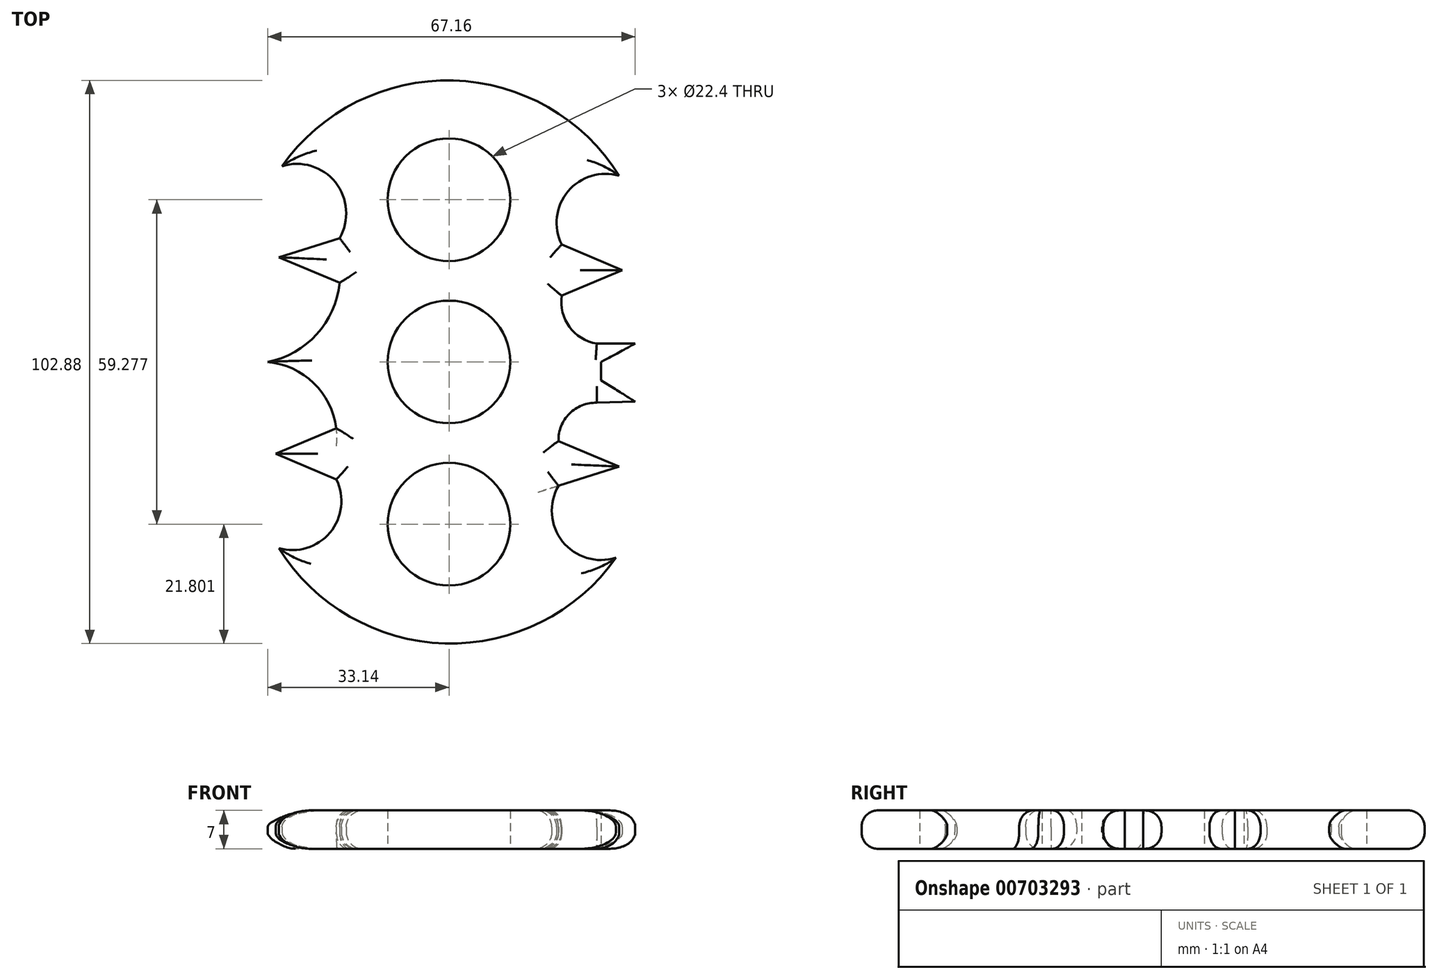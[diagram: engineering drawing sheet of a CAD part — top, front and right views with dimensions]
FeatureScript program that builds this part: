
annotation { "Feature Type Name" : "Feature", "Feature Type Description" : "" }
export const myFeature = defineFeature(function(context is Context, id is Id, definition is map)
    precondition{}
    {
        {
            var Q0;
            Q0=qCreatedBy(makeId("Top.planeOp"),FACE);
            var sketch = newSketch(context, id + "F0", { "sketchPlane" : qUnion([Q0])});
            skCircle(sketch, "E0", {"center": v(0, 0) * mm, "radius": 11.2 * mm});
            skCircle(sketch, "E1", {"center": v(0, 29.64) * mm, "radius": 11.2 * mm});
            skCircle(sketch, "E2.1.1", {"center": v(0, -29.64) * mm, "radius": 11.2 * mm});
            skArc(sketch, "E3", {"start": v(31.1, 34.02) * mm, "mid": v(0.76, 51.42) * mm, "end": v(-30.51, 35.77) * mm});
            skArc(sketch, "E4", {"start": v(-20, 22.63) * mm, "mid": v(-20.75, 32.8) * mm, "end": v(-30.51, 35.77) * mm});
            skLineSegment(sketch, "E5", {"start": v(-20, 22.63) * mm, "end": v(-31.1, 19.13) * mm});
            skLineSegment(sketch, "E6", {"start": v(-31.1, 19.13) * mm, "end": v(-20, 14.45) * mm});
            skArc(sketch, "E7", {"start": v(-33.14, 0) * mm, "mid": v(-24.17, 5.05) * mm, "end": v(-20, 14.45) * mm});
            skArc(sketch, "E8.1.0", {"start": v(-31.1, -34.02) * mm, "mid": v(-0.76, -51.42) * mm, "end": v(30.51, -35.77) * mm});
            skArc(sketch, "E8.1.1", {"start": v(20, -22.63) * mm, "mid": v(20.75, -32.8) * mm, "end": v(30.51, -35.77) * mm});
            skLineSegment(sketch, "E8.1.2", {"start": v(20, -22.63) * mm, "end": v(31.1, -19.13) * mm});
            skLineSegment(sketch, "E8.1.3", {"start": v(31.1, -19.13) * mm, "end": v(20, -14.45) * mm});
            skArc(sketch, "E9", {"start": v(-20.59, -12.12) * mm, "mid": v(-24.73, -3.85) * mm, "end": v(-33.14, 0) * mm});
            skLineSegment(sketch, "E10", {"start": v(-20.59, -12.12) * mm, "end": v(-31.68, -16.8) * mm});
            skLineSegment(sketch, "E11", {"start": v(-31.68, -16.8) * mm, "end": v(-20.59, -21.46) * mm});
            skArc(sketch, "E12", {"start": v(-31.1, -34.02) * mm, "mid": v(-21.74, -31.17) * mm, "end": v(-20.59, -21.46) * mm});
            skLineSegment(sketch, "E13.1.0", {"start": v(20.59, 12.12) * mm, "end": v(31.68, 16.8) * mm});
            skLineSegment(sketch, "E13.1.1", {"start": v(31.68, 16.8) * mm, "end": v(20.59, 21.46) * mm});
            skArc(sketch, "E13.1.2", {"start": v(31.1, 34.02) * mm, "mid": v(21.74, 31.17) * mm, "end": v(20.59, 21.46) * mm});
            skArc(sketch, "E14", {"start": v(20.59, 12.12) * mm, "mid": v(22, 6.42) * mm, "end": v(27.01, 3.36) * mm});
            skArc(sketch, "E15", {"start": v(27.01, -7.45) * mm, "mid": v(22.01, -9.45) * mm, "end": v(20, -14.45) * mm});
            skLineSegment(sketch, "E16", {"start": v(27.01, 3.36) * mm, "end": v(34.02, 3.36) * mm});
            skLineSegment(sketch, "E17", {"start": v(34.02, 3.36) * mm, "end": v(27.8, 0) * mm});
            skLineSegment(sketch, "E18", {"start": v(27.8, 0) * mm, "end": v(27.8, -3.36) * mm});
            skLineSegment(sketch, "E19", {"start": v(27.8, -3.36) * mm, "end": v(34.02, -7.26) * mm});
            skLineSegment(sketch, "E20", {"start": v(34.02, -7.26) * mm, "end": v(27.01, -7.45) * mm});
            skSolve(sketch);
        }
        {
            var Q0;
            Q0=makeQuery(id+"F0.imprint","IMPRINT",FACE,{"disambiguationData":[TD([[makeQuery(id+"F0.imprint","IMPRINT",EDGE,{"derivedFrom":sQuery(id+"F0.wireOp",EDGE,"E0")}),-1.0]])]});
            extrude(context, id + "F1", {"entities" : qUnion([Q0]), "depth" : 7 * mm, "offsetDistance" : 25 * mm});
        }
        {
            var Q0;
            Q0=makeQuery(id+"F1.opExtrude","CAP_EDGE",EDGE,{"disambiguationData":[OSD([sQuery(id+"F0.wireOp",EDGE,"E3")])],"isStart":false});
            var Q1;
            Q1=makeQuery(id+"F1.opExtrude","CAP_EDGE",EDGE,{"disambiguationData":[OSD([sQuery(id+"F0.wireOp",EDGE,"E8.1.0")])],"isStart":false});
            var Q2;
            Q2=makeQuery(id+"F1.opExtrude","CAP_EDGE",EDGE,{"disambiguationData":[OSD([sQuery(id+"F0.wireOp",EDGE,"E12")])],"isStart":false});
            var Q3;
            Q3=makeQuery(id+"F1.opExtrude","CAP_EDGE",EDGE,{"disambiguationData":[OSD([sQuery(id+"F0.wireOp",EDGE,"E8.1.1")])],"isStart":false});
            var Q4;
            Q4=makeQuery(id+"F1.opExtrude","CAP_EDGE",EDGE,{"disambiguationData":[OSD([sQuery(id+"F0.wireOp",EDGE,"E14")])],"isStart":false});
            var Q5;
            Q5=makeQuery(id+"F1.opExtrude","CAP_EDGE",EDGE,{"disambiguationData":[OSD([sQuery(id+"F0.wireOp",EDGE,"E15")])],"isStart":false});
            var Q6;
            Q6=makeQuery(id+"F1.opExtrude","CAP_EDGE",EDGE,{"disambiguationData":[OSD([sQuery(id+"F0.wireOp",EDGE,"E16")])],"isStart":false});
            var Q7;
            Q7=makeQuery(id+"F1.opExtrude","CAP_EDGE",EDGE,{"disambiguationData":[OSD([sQuery(id+"F0.wireOp",EDGE,"E13.1.2")])],"isStart":false});
            var Q8;
            Q8=makeQuery(id+"F1.opExtrude","CAP_EDGE",EDGE,{"disambiguationData":[OSD([sQuery(id+"F0.wireOp",EDGE,"E20")])],"isStart":false});
            var Q9;
            Q9=makeQuery(id+"F1.opExtrude","CAP_EDGE",EDGE,{"disambiguationData":[OSD([sQuery(id+"F0.wireOp",EDGE,"E9")])],"isStart":false});
            var Q10;
            Q10=makeQuery(id+"F1.opExtrude","CAP_EDGE",EDGE,{"disambiguationData":[OSD([sQuery(id+"F0.wireOp",EDGE,"E7")])],"isStart":false});
            var Q11;
            Q11=makeQuery(id+"F1.opExtrude","CAP_EDGE",EDGE,{"disambiguationData":[OSD([sQuery(id+"F0.wireOp",EDGE,"E6")])],"isStart":false});
            var Q12;
            Q12=makeQuery(id+"F1.opExtrude","CAP_EDGE",EDGE,{"disambiguationData":[OSD([sQuery(id+"F0.wireOp",EDGE,"E4")])],"isStart":false});
            var Q13;
            Q13=makeQuery(id+"F1.opExtrude","CAP_EDGE",EDGE,{"disambiguationData":[OSD([sQuery(id+"F0.wireOp",EDGE,"E5")])],"isStart":false});
            var Q14;
            Q14=makeQuery(id+"F1.opExtrude","CAP_EDGE",EDGE,{"disambiguationData":[OSD([sQuery(id+"F0.wireOp",EDGE,"E10")])],"isStart":false});
            var Q15;
            Q15=makeQuery(id+"F1.opExtrude","CAP_EDGE",EDGE,{"disambiguationData":[OSD([sQuery(id+"F0.wireOp",EDGE,"E8.1.3")])],"isStart":false});
            var Q16;
            Q16=makeQuery(id+"F1.opExtrude","CAP_EDGE",EDGE,{"disambiguationData":[OSD([sQuery(id+"F0.wireOp",EDGE,"E11")])],"isStart":false});
            var Q17;
            Q17=makeQuery(id+"F1.opExtrude","CAP_EDGE",EDGE,{"disambiguationData":[OSD([sQuery(id+"F0.wireOp",EDGE,"E8.1.2")])],"isStart":false});
            var Q18;
            Q18=makeQuery(id+"F1.opExtrude","CAP_EDGE",EDGE,{"disambiguationData":[OSD([sQuery(id+"F0.wireOp",EDGE,"E13.1.1")])],"isStart":false});
            var Q19;
            Q19=makeQuery(id+"F1.opExtrude","CAP_EDGE",EDGE,{"disambiguationData":[OSD([sQuery(id+"F0.wireOp",EDGE,"E13.1.0")])],"isStart":false});
            var Q20;
            Q20=makeQuery(id+"F1.opExtrude","CAP_EDGE",EDGE,{"disambiguationData":[OSD([sQuery(id+"F0.wireOp",EDGE,"E8.1.0")])],"isStart":true});
            var Q21;
            Q21=makeQuery(id+"F1.opExtrude","CAP_EDGE",EDGE,{"disambiguationData":[OSD([sQuery(id+"F0.wireOp",EDGE,"E3")])],"isStart":true});
            var Q22;
            Q22=makeQuery(id+"F1.opExtrude","CAP_EDGE",EDGE,{"disambiguationData":[OSD([sQuery(id+"F0.wireOp",EDGE,"E20")])],"isStart":true});
            var Q23;
            Q23=makeQuery(id+"F1.opExtrude","CAP_EDGE",EDGE,{"disambiguationData":[OSD([sQuery(id+"F0.wireOp",EDGE,"E15")])],"isStart":true});
            var Q24;
            Q24=makeQuery(id+"F1.opExtrude","CAP_EDGE",EDGE,{"disambiguationData":[OSD([sQuery(id+"F0.wireOp",EDGE,"E14")])],"isStart":true});
            var Q25;
            Q25=makeQuery(id+"F1.opExtrude","CAP_EDGE",EDGE,{"disambiguationData":[OSD([sQuery(id+"F0.wireOp",EDGE,"E16")])],"isStart":true});
            var Q26;
            Q26=makeQuery(id+"F1.opExtrude","CAP_EDGE",EDGE,{"disambiguationData":[OSD([sQuery(id+"F0.wireOp",EDGE,"E8.1.3")])],"isStart":true});
            var Q27;
            Q27=makeQuery(id+"F1.opExtrude","CAP_EDGE",EDGE,{"disambiguationData":[OSD([sQuery(id+"F0.wireOp",EDGE,"E8.1.1")])],"isStart":true});
            var Q28;
            Q28=makeQuery(id+"F1.opExtrude","CAP_EDGE",EDGE,{"disambiguationData":[OSD([sQuery(id+"F0.wireOp",EDGE,"E12")])],"isStart":true});
            var Q29;
            Q29=makeQuery(id+"F1.opExtrude","CAP_EDGE",EDGE,{"disambiguationData":[OSD([sQuery(id+"F0.wireOp",EDGE,"E11")])],"isStart":true});
            var Q30;
            Q30=makeQuery(id+"F1.opExtrude","CAP_EDGE",EDGE,{"disambiguationData":[OSD([sQuery(id+"F0.wireOp",EDGE,"E10")])],"isStart":true});
            var Q31;
            Q31=makeQuery(id+"F1.opExtrude","CAP_EDGE",EDGE,{"disambiguationData":[OSD([sQuery(id+"F0.wireOp",EDGE,"E7")])],"isStart":true});
            var Q32;
            Q32=makeQuery(id+"F1.opExtrude","CAP_EDGE",EDGE,{"disambiguationData":[OSD([sQuery(id+"F0.wireOp",EDGE,"E6")])],"isStart":true});
            var Q33;
            Q33=makeQuery(id+"F1.opExtrude","CAP_EDGE",EDGE,{"disambiguationData":[OSD([sQuery(id+"F0.wireOp",EDGE,"E5")])],"isStart":true});
            var Q34;
            Q34=makeQuery(id+"F1.opExtrude","CAP_EDGE",EDGE,{"disambiguationData":[OSD([sQuery(id+"F0.wireOp",EDGE,"E4")])],"isStart":true});
            var Q35;
            Q35=makeQuery(id+"F1.opExtrude","CAP_EDGE",EDGE,{"disambiguationData":[OSD([sQuery(id+"F0.wireOp",EDGE,"E13.1.2")])],"isStart":true});
            var Q36;
            Q36=makeQuery(id+"F1.opExtrude","CAP_EDGE",EDGE,{"disambiguationData":[OSD([sQuery(id+"F0.wireOp",EDGE,"E13.1.1")])],"isStart":true});
            var Q37;
            Q37=makeQuery(id+"F1.opExtrude","CAP_EDGE",EDGE,{"disambiguationData":[OSD([sQuery(id+"F0.wireOp",EDGE,"E13.1.0")])],"isStart":true});
            fillet(context, id + "F2", {"entities" : qUnion([Q0, Q1, Q2, Q3, Q4, Q5, Q6, Q7, Q8, Q9, Q10, Q11, Q12, Q13, Q14, Q15, Q16, Q17, Q18, Q19, Q20, Q21, Q22, Q23, Q24, Q25, Q26, Q27, Q28, Q29, Q30, Q31, Q32, Q33, Q34, Q35, Q36, Q37]), "radius" : 3 * mm, "tangentPropagation" : true, "allowEdgeOverflow" : false});
        }
    });
